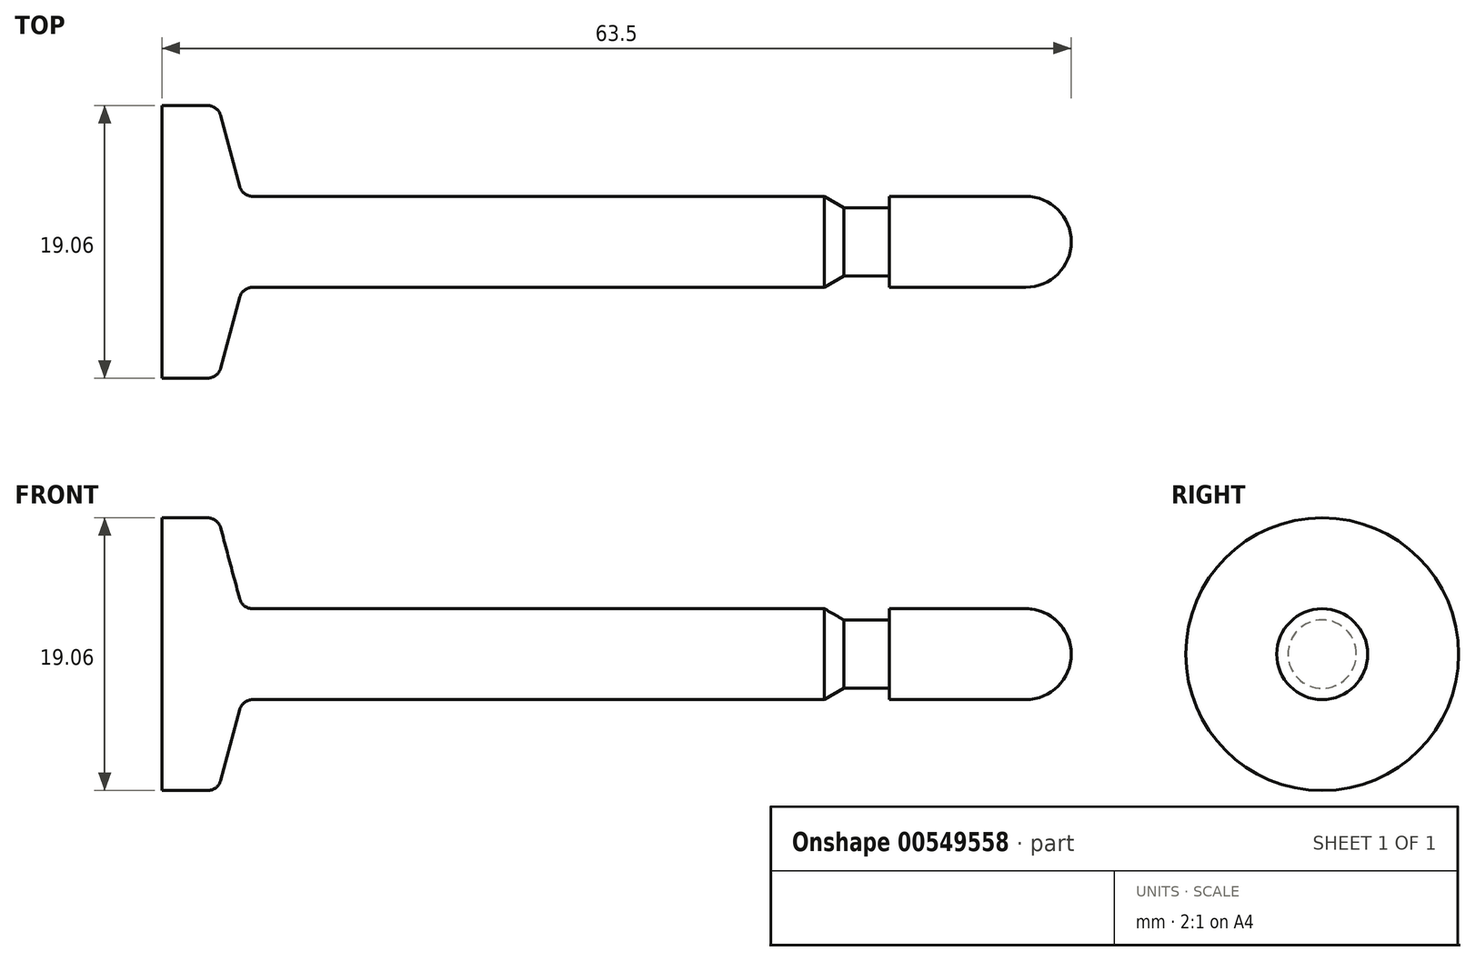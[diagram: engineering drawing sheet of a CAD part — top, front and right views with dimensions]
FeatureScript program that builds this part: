
annotation { "Feature Type Name" : "Feature", "Feature Type Description" : "" }
export const myFeature = defineFeature(function(context is Context, id is Id, definition is map)
    precondition{}
    {
        {
            var Q0;
            Q0=qCreatedBy(makeId("Front.planeOp"),FACE);
            var sketch = newSketch(context, id + "F0", { "sketchPlane" : qUnion([Q0])});
            skLineSegment(sketch, "E0", {"start": v(-76.25, 0) * mm, "end": v(0, 0) * mm, "construction": true});
            skLineSegment(sketch, "E1", {"start": v(-63.5, 0) * mm, "end": v(-63.5, 9.53) * mm});
            skLineSegment(sketch, "E2", {"start": v(-63.5, 9.53) * mm, "end": v(-60.33, 9.53) * mm});
            skLineSegment(sketch, "E3", {"start": v(-59.4, 8.82) * mm, "end": v(-58.08, 3.88) * mm});
            skLineSegment(sketch, "E4", {"start": v(-57.16, 3.18) * mm, "end": v(-17.24, 3.18) * mm});
            skLineSegment(sketch, "E5", {"start": v(-17.24, 3.18) * mm, "end": v(-15.88, 2.39) * mm});
            skLineSegment(sketch, "E6", {"start": v(-15.88, 2.39) * mm, "end": v(-12.7, 2.39) * mm});
            skLineSegment(sketch, "E7", {"start": v(-12.7, 2.39) * mm, "end": v(-12.7, 3.18) * mm});
            skLineSegment(sketch, "E8", {"start": v(-12.7, 3.18) * mm, "end": v(-3.18, 3.18) * mm});
            skLineSegment(sketch, "E9", {"start": v(0, 0) * mm, "end": v(-63.5, 0) * mm});
            skPoint(sketch, "E10.visualSharp", {"position": v(-59.6, 9.53) * mm});
            skArc(sketch, "E10.filletArc", {"start": v(-59.4, 8.82) * mm, "mid": v(-59.75, 9.33) * mm, "end": v(-60.33, 9.53) * mm});
            skPoint(sketch, "E11.visualSharp", {"position": v(-57.9, 3.18) * mm});
            skArc(sketch, "E11.filletArc", {"start": v(-58.08, 3.88) * mm, "mid": v(-57.74, 3.37) * mm, "end": v(-57.16, 3.17) * mm});
            skLineSegment(sketch, "E12", {"start": v(0, 0) * mm, "end": v(0, 0) * mm});
            skArc(sketch, "E13.filletArc", {"start": v(0, 0) * mm, "mid": v(-0.93, 2.25) * mm, "end": v(-3.18, 3.17) * mm});
            skSolve(sketch);
        }
        {
            var Q0;
            Q0=makeQuery(id+"F0.imprint","IMPRINT",FACE,{"disambiguationData":[TD([[makeQuery(id+"F0.imprint","IMPRINT",EDGE,{"derivedFrom":sQuery(id+"F0.wireOp",EDGE,"E1")}),-1.0]])]});
            var Q1;
            Q1=sQuery(id+"F0.wireOp",EDGE,"E0");
            revolve(context, id + "F1", {"entities" : qUnion([Q0]), "axis" : qUnion([Q1]), "revolveType" : RevolveType.FULL});
        }
    });
